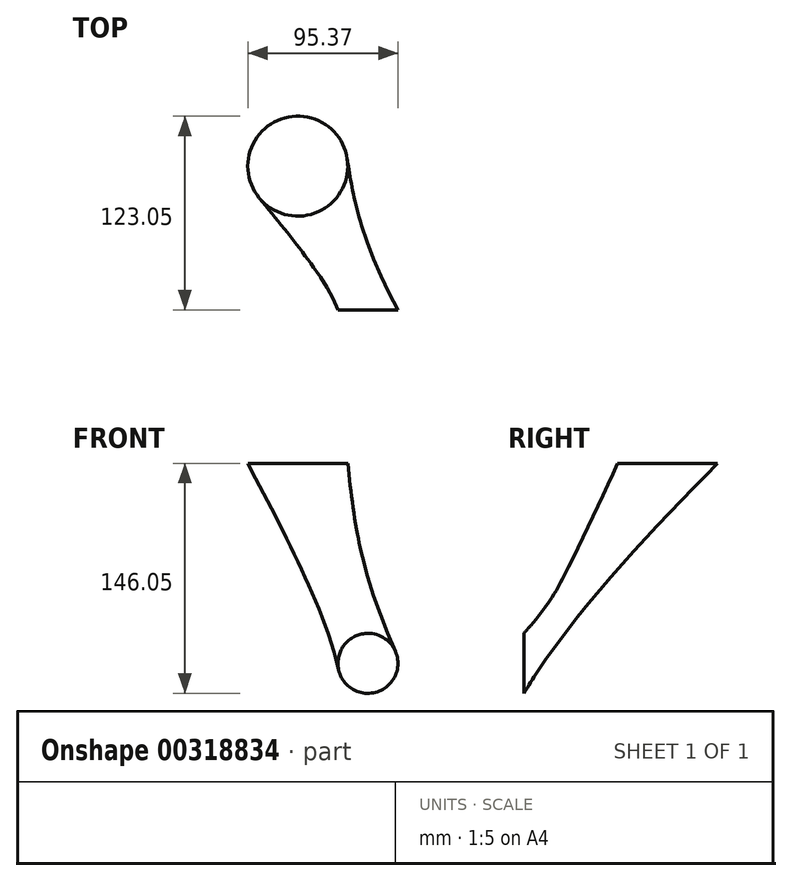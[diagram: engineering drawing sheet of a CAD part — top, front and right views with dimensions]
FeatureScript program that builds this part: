
annotation { "Feature Type Name" : "Feature", "Feature Type Description" : "" }
export const myFeature = defineFeature(function(context is Context, id is Id, definition is map)
    precondition{}
    {
        {
            var Q0;
            Q0=qCreatedBy(makeId("Top.planeOp"),FACE);
            cPlane(context, id + "F0", {"entities" : qUnion([Q0]), "cplaneType" : CPlaneType.OFFSET, "offset" : 127 * mm, "width" : 152.4 * mm, "height" : 152.4 * mm});
        }
        {
            var Q0;
            Q0=qCreatedBy(makeId("Front.planeOp"),FACE);
            var sketch = newSketch(context, id + "F1", { "sketchPlane" : qUnion([Q0])});
            skCircle(sketch, "E0", {"center": v(0, 0) * mm, "radius": 19.05 * mm});
            skSolve(sketch);
        }
        {
            var Q0;
            Q0=qCreatedBy(id+"F0.planeOp",FACE);
            var sketch = newSketch(context, id + "F2", { "sketchPlane" : qUnion([Q0])});
            skCircle(sketch, "E1", {"center": v(-44.57, 91.3) * mm, "radius": 31.75 * mm});
            skSolve(sketch);
        }
        {
            var Q0;
            Q0=makeQuery(id+"F2.imprint","IMPRINT",FACE,{"disambiguationData":[TD([[makeQuery(id+"F2.imprint","IMPRINT",EDGE,{"derivedFrom":sQuery(id+"F2.wireOp",EDGE,"E1")}),1.0]])]});
            var Q1;
            Q1=makeQuery(id+"F1.imprint","IMPRINT",FACE,{"disambiguationData":[TD([[makeQuery(id+"F1.imprint","IMPRINT",EDGE,{"derivedFrom":sQuery(id+"F1.wireOp",EDGE,"E0")}),1.0]])]});
            loft(context, id + "F3", {"sheetProfilesArray" : [{ "sheetProfileEntities" : qUnion([Q0]) }, { "sheetProfileEntities" : qUnion([Q1]) }]});
        }
    });
